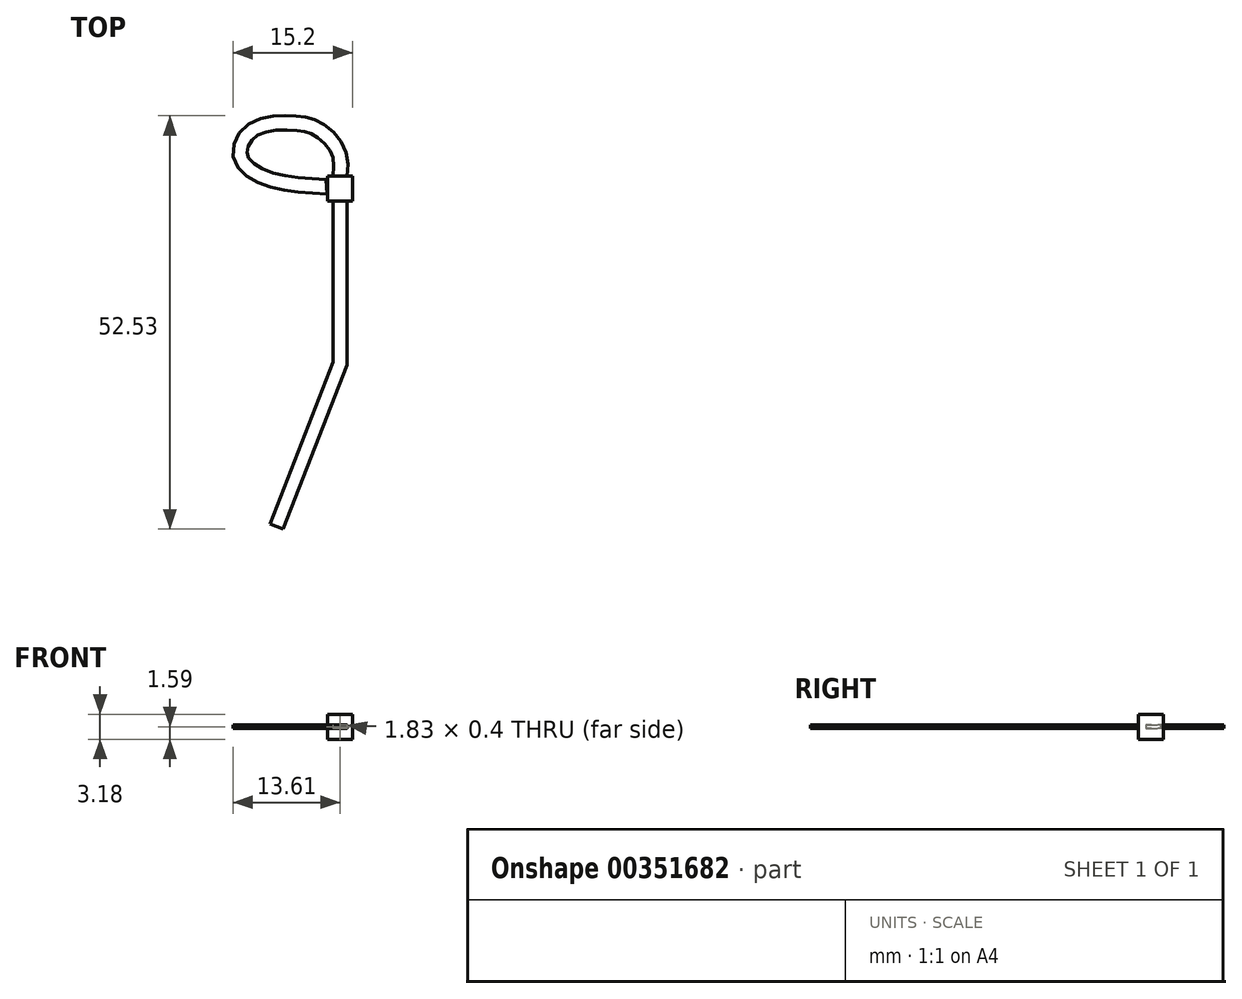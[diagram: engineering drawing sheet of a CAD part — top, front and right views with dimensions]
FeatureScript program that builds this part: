
annotation { "Feature Type Name" : "Feature", "Feature Type Description" : "" }
export const myFeature = defineFeature(function(context is Context, id is Id, definition is map)
    precondition{}
    {
        {
            var Q0;
            Q0=qCreatedBy(makeId("Front.planeOp"),FACE);
            var sketch = newSketch(context, id + "F0", { "sketchPlane" : qUnion([Q0])});
            skLineSegment(sketch, "E0.bottom", {"start": v(-1.59, 1.59) * mm, "end": v(1.59, 1.59) * mm});
            skLineSegment(sketch, "E0.top", {"start": v(-1.59, -1.59) * mm, "end": v(1.59, -1.59) * mm});
            skLineSegment(sketch, "E0.left", {"start": v(-1.59, 1.59) * mm, "end": v(-1.59, -1.59) * mm});
            skLineSegment(sketch, "E0.right", {"start": v(1.59, 1.59) * mm, "end": v(1.59, -1.59) * mm});
            skPoint(sketch, "E0.middle", {"position": v(0, 0) * mm});
            skSolve(sketch);
        }
        {
            var Q0;
            Q0 = qSketchRegion(id + "F0", true);
            extrude(context, id + "F1", {"entities" : qUnion([Q0]), "endBound" : BoundingType.SYMMETRIC, "depth" : 3.17 * mm});
        }
        {
            var Q0;
            Q0=makeQuery(id+"F1.opExtrude","CAP_FACE",FACE,{"disambiguationData":[OSD([sQuery(id+"F0.wireOp",EDGE,"E0.bottom"),sQuery(id+"F0.wireOp",EDGE,"E0.top"),sQuery(id+"F0.wireOp",EDGE,"E0.left"),sQuery(id+"F0.wireOp",EDGE,"E0.right")])],"isStart":false});
            var sketch = newSketch(context, id + "F2", { "sketchPlane" : qUnion([Q0])});
            skLineSegment(sketch, "E1.bottom", {"start": v(-0.91, 0.2) * mm, "end": v(0.91, 0.2) * mm});
            skLineSegment(sketch, "E1.top", {"start": v(-0.91, -0.2) * mm, "end": v(0.91, -0.2) * mm});
            skLineSegment(sketch, "E1.left", {"start": v(-0.91, 0.2) * mm, "end": v(-0.91, -0.2) * mm});
            skLineSegment(sketch, "E1.right", {"start": v(0.91, 0.2) * mm, "end": v(0.91, -0.2) * mm});
            skPoint(sketch, "E1.middle", {"position": v(0, 0) * mm});
            skSolve(sketch);
        }
        {
            var Q0;
            Q0=qCreatedBy(makeId("Top.planeOp"),FACE);
            var sketch = newSketch(context, id + "F3", { "sketchPlane" : qUnion([Q0])});
            skLineSegment(sketch, "E2", {"start": v(0, 0) * mm, "end": v(0, -22.23) * mm});
            skLineSegment(sketch, "E3", {"start": v(0, -22.23) * mm, "end": v(-8.07, -42.93) * mm});
            skFitSpline(sketch, "E4", {"points": [v(0, 0) * mm, v(0, 4.81) * mm, v(-3.03, 7.95) * mm, v(-6.17, 8.58) * mm, v(-11.3, 7.63) * mm, v(-12.86, 3.97) * mm, v(-9.3, 1.05) * mm, v(-1.67, 0) * mm], "startDerivative": vector(5.95, 35.12) * mm, "endDerivative": vector(44.44, -2.23) * mm});
            skSolve(sketch);
        }
        {
            var Q0;
            Q0=makeQuery(id+"F2.imprint","IMPRINT",FACE,{"disambiguationData":[TD([[makeQuery(id+"F2.imprint","IMPRINT",EDGE,{"derivedFrom":sQuery(id+"F2.wireOp",EDGE,"E1.bottom")}),-1.0]])]});
            var Q1;
            Q1=sQuery(id+"F3.wireOp",EDGE,"E2");
            var Q2;
            Q2=sQuery(id+"F3.wireOp",EDGE,"E3");
            sweep(context, id + "F4", {"operationType" : NewBodyOperationType.ADD, "profiles" : qUnion([Q0]), "path" : qUnion([Q1, Q2])});
        }
        {
            var Q0;
            Q0=makeQuery(id+"F1.opExtrude","CAP_FACE",FACE,{"disambiguationData":[OSD([sQuery(id+"F0.wireOp",EDGE,"E0.bottom"),sQuery(id+"F0.wireOp",EDGE,"E0.top"),sQuery(id+"F0.wireOp",EDGE,"E0.left"),sQuery(id+"F0.wireOp",EDGE,"E0.right")])],"isStart":true});
            var sketch = newSketch(context, id + "F5", { "sketchPlane" : qUnion([Q0])});
            skLineSegment(sketch, "E5.bottom", {"start": v(-0.91, 0.2) * mm, "end": v(0.91, 0.2) * mm});
            skLineSegment(sketch, "E5.top", {"start": v(-0.91, -0.2) * mm, "end": v(0.91, -0.2) * mm});
            skLineSegment(sketch, "E5.left", {"start": v(-0.91, 0.2) * mm, "end": v(-0.91, -0.2) * mm});
            skLineSegment(sketch, "E5.right", {"start": v(0.91, 0.2) * mm, "end": v(0.91, -0.2) * mm});
            skPoint(sketch, "E5.middle", {"position": v(0, 0) * mm});
            skSolve(sketch);
        }
        {
            var Q0;
            Q0=makeQuery(id+"F5.imprint","IMPRINT",FACE,{"disambiguationData":[TD([[makeQuery(id+"F5.imprint","IMPRINT",EDGE,{"derivedFrom":sQuery(id+"F5.wireOp",EDGE,"E5.bottom")}),-1.0]])]});
            var Q1;
            Q1=sQuery(id+"F3.wireOp",EDGE,"E4");
            sweep(context, id + "F6", {"operationType" : NewBodyOperationType.ADD, "profiles" : qUnion([Q0]), "path" : qUnion([Q1])});
        }
    });
